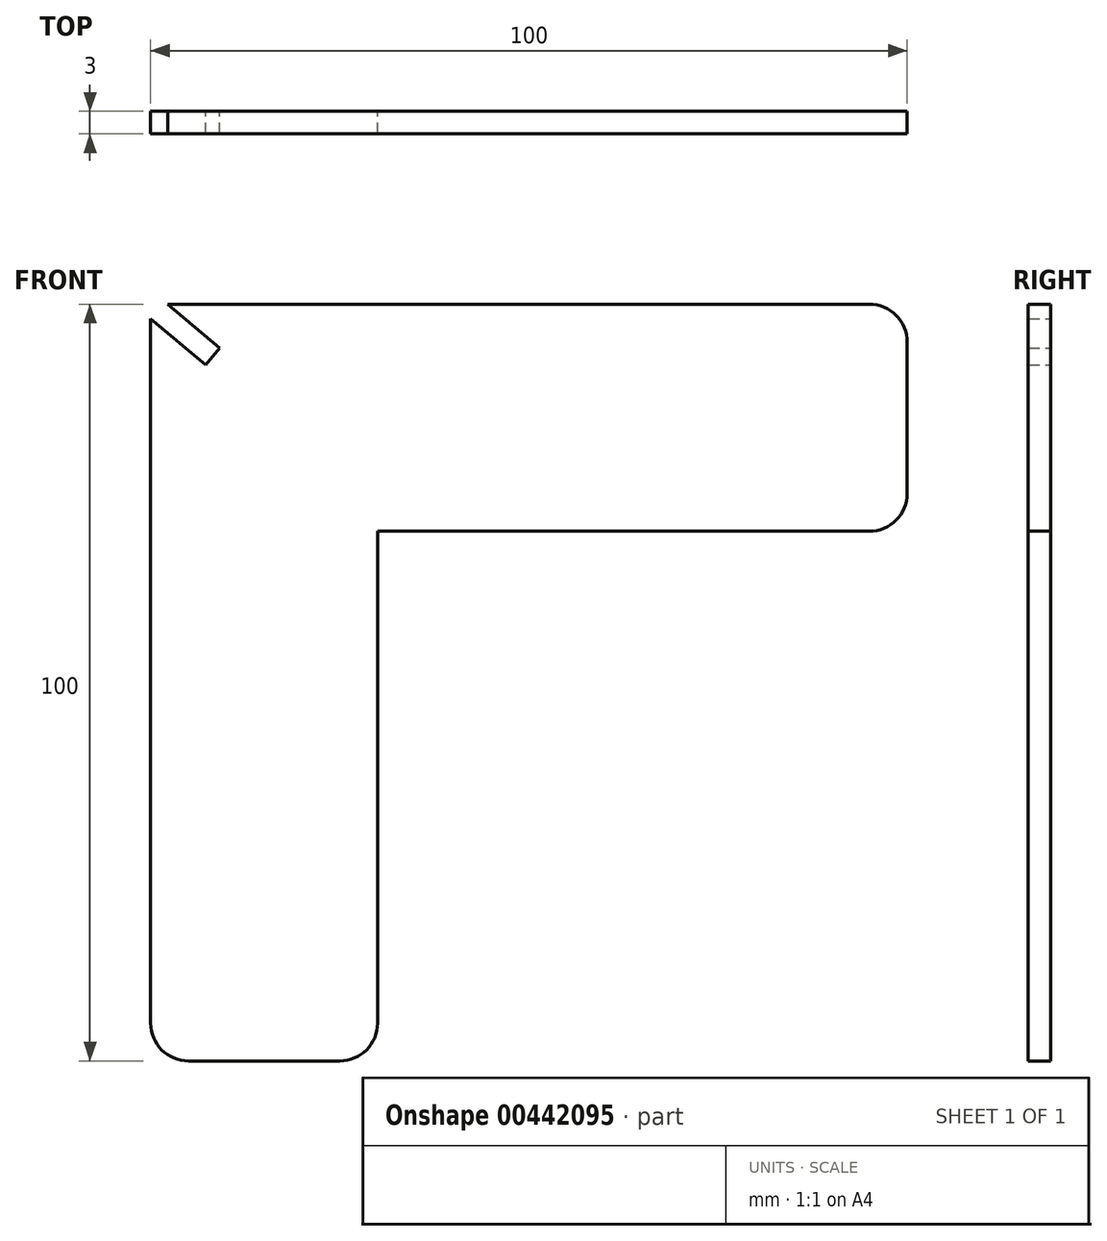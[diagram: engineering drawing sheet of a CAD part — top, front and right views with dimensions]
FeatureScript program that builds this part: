
annotation { "Feature Type Name" : "Feature", "Feature Type Description" : "" }
export const myFeature = defineFeature(function(context is Context, id is Id, definition is map)
    precondition{}
    {
        {
            var Q0;
            Q0=qCreatedBy(makeId("Front.planeOp"),FACE);
            var sketch = newSketch(context, id + "F0", { "sketchPlane" : qUnion([Q0])});
            skLineSegment(sketch, "E0.bottom", {"start": v(0, 74.58) * mm, "end": v(-27.74, 74.58) * mm});
            skLineSegment(sketch, "E0.top", {"start": v(-5, -25.42) * mm, "end": v(-25, -25.42) * mm});
            skLineSegment(sketch, "E0.left", {"start": v(0, 44.58) * mm, "end": v(0, -20.42) * mm});
            skLineSegment(sketch, "E0.right", {"start": v(-30, 72.69) * mm, "end": v(-30, -20.42) * mm});
            skLineSegment(sketch, "E1.bottom", {"start": v(-27.74, 74.58) * mm, "end": v(65, 74.58) * mm});
            skLineSegment(sketch, "E1.top", {"start": v(0, 44.58) * mm, "end": v(65, 44.58) * mm});
            skLineSegment(sketch, "E1.left", {"start": v(-30, 72.69) * mm, "end": v(-30, 44.58) * mm});
            skLineSegment(sketch, "E1.right", {"start": v(70, 69.58) * mm, "end": v(70, 49.58) * mm});
            skPoint(sketch, "E2.visualSharp", {"position": v(70, 74.58) * mm});
            skArc(sketch, "E2.filletArc", {"start": v(70, 69.58) * mm, "mid": v(68.54, 73.11) * mm, "end": v(65, 74.58) * mm});
            skPoint(sketch, "E3.visualSharp", {"position": v(70, 44.58) * mm});
            skArc(sketch, "E3.filletArc", {"start": v(65, 44.58) * mm, "mid": v(68.54, 46.04) * mm, "end": v(70, 49.58) * mm});
            skPoint(sketch, "E4.visualSharp", {"position": v(-30, -25.42) * mm});
            skArc(sketch, "E4.filletArc", {"start": v(-30, -20.42) * mm, "mid": v(-28.54, -23.96) * mm, "end": v(-25, -25.42) * mm});
            skPoint(sketch, "E5.visualSharp", {"position": v(0, -25.42) * mm});
            skArc(sketch, "E5.filletArc", {"start": v(-5, -25.42) * mm, "mid": v(-1.46, -23.96) * mm, "end": v(0, -20.42) * mm});
            skLineSegment(sketch, "E6.bottom", {"start": v(-20.87, 68.81) * mm, "end": v(-22.73, 66.59) * mm});
            skLineSegment(sketch, "E6.left", {"start": v(-20.87, 68.81) * mm, "end": v(-27.74, 74.58) * mm});
            skLineSegment(sketch, "E6.right", {"start": v(-22.73, 66.59) * mm, "end": v(-30, 72.69) * mm});
            skPoint(sketch, "E6.middle", {"position": v(-30, 74.58) * mm});
            skPoint(sketch, "E6.top.start.orphan", {"position": v(-37.27, 82.57) * mm});
            skPoint(sketch, "E7.orphan", {"position": v(-39.13, 80.35) * mm});
            skSolve(sketch);
        }
        {
            var Q0;
            {var subQ5=sQuery(id+"F0.wireOp",EDGE,"E1.left");Q0=makeQuery(id+"F0.imprint","IMPRINT",FACE,{"disambiguationData":[TD([[makeQuery(id+"F0.imprint","IMPRINT",EDGE,{"derivedFrom":subQ5}),1.0]])]});}
            var Q1;
            Q1=makeQuery(id+"F0.imprint","IMPRINT",FACE,{"disambiguationData":[TD([[makeQuery(id+"F0.imprint","IMPRINT",EDGE,{"derivedFrom":sQuery(id+"F0.wireOp",EDGE,"E0.top")}),-1.0]])]});
            var Q2;
            Q2=makeQuery(id+"F0.imprint","IMPRINT",FACE,{"disambiguationData":[TD([[makeQuery(id+"F0.imprint","IMPRINT",EDGE,{"derivedFrom":sQuery(id+"F0.wireOp",EDGE,"E1.right")}),-1.0]])]});
            extrude(context, id + "F1", {"entities" : qUnion([Q0, Q1, Q2]), "depth" : 3 * mm});
        }
    });
